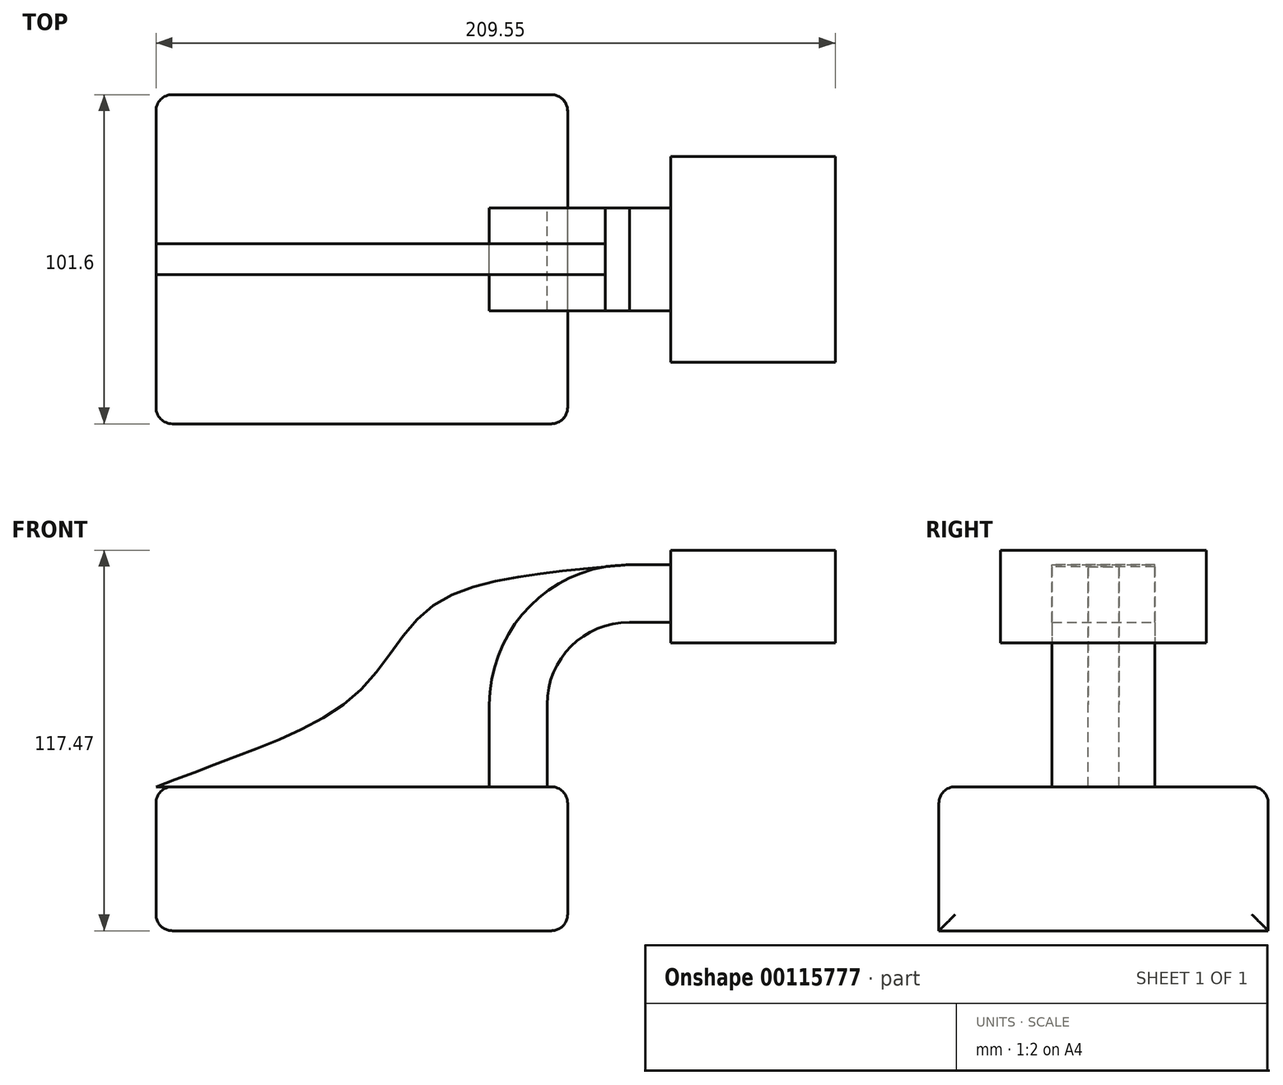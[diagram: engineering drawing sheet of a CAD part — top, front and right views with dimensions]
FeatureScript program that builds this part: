
annotation { "Feature Type Name" : "Feature", "Feature Type Description" : "" }
export const myFeature = defineFeature(function(context is Context, id is Id, definition is map)
    precondition{}
    {
        {
            var Q0;
            Q0=qCreatedBy(makeId("Front.planeOp"),FACE);
            var sketch = newSketch(context, id + "F0", { "sketchPlane" : qUnion([Q0])});
            skLineSegment(sketch, "E0.bottom", {"start": v(0, 0) * mm, "end": v(127, 0) * mm});
            skLineSegment(sketch, "E0.top", {"start": v(0, 44.45) * mm, "end": v(127, 44.45) * mm});
            skLineSegment(sketch, "E0.left", {"start": v(0, 0) * mm, "end": v(0, 44.45) * mm});
            skLineSegment(sketch, "E0.right", {"start": v(127, 0) * mm, "end": v(127, 44.45) * mm});
            skLineSegment(sketch, "E1.bottom", {"start": v(158.75, 88.9) * mm, "end": v(209.55, 88.9) * mm});
            skLineSegment(sketch, "E1.top", {"start": v(158.75, 117.48) * mm, "end": v(209.55, 117.48) * mm});
            skLineSegment(sketch, "E1.left", {"start": v(158.75, 88.9) * mm, "end": v(158.75, 117.48) * mm});
            skLineSegment(sketch, "E1.right", {"start": v(209.55, 88.9) * mm, "end": v(209.55, 117.48) * mm});
            skLineSegment(sketch, "E2", {"start": v(120.65, 44.45) * mm, "end": v(120.65, 69.85) * mm});
            skLineSegment(sketch, "E3", {"start": v(146.05, 95.25) * mm, "end": v(158.75, 95.25) * mm});
            skArc(sketch, "E4", {"start": v(120.65, 69.85) * mm, "mid": v(128.09, 87.81) * mm, "end": v(146.05, 95.25) * mm});
            skLineSegment(sketch, "E5.0", {"start": v(146.05, 113.03) * mm, "end": v(158.75, 113.03) * mm});
            skArc(sketch, "E5.1", {"start": v(102.87, 69.85) * mm, "mid": v(115.52, 100.38) * mm, "end": v(146.05, 113.03) * mm});
            skLineSegment(sketch, "E5.2", {"start": v(102.87, 44.45) * mm, "end": v(102.87, 69.85) * mm});
            skPoint(sketch, "E6", {"position": v(114.9, 109.67) * mm});
            skPoint(sketch, "E7", {"position": v(83.78, 99.03) * mm});
            skPoint(sketch, "E8", {"position": v(62.5, 73.65) * mm});
            skPoint(sketch, "E9", {"position": v(28.52, 55.23) * mm});
            skFitSpline(sketch, "E10", {"points": [v(0, 44.45) * mm, v(28.52, 55.23) * mm, v(62.5, 73.65) * mm, v(83.78, 99.03) * mm, v(114.9, 109.67) * mm, v(146.05, 113.03) * mm], "startDerivative": vector(142.18, 53.02) * mm, "endDerivative": vector(157.03, 13.52) * mm});
            skSolve(sketch);
        }
        {
            var Q0;
            Q0=makeQuery(id+"F0.imprint","IMPRINT",FACE,{"disambiguationData":[TD([[makeQuery(id+"F0.imprint","IMPRINT",EDGE,{"derivedFrom":sQuery(id+"F0.wireOp",EDGE,"E0.bottom")}),1.0]])]});
            extrude(context, id + "F1", {"entities" : qUnion([Q0]), "endBound" : BoundingType.SYMMETRIC, "depth" : 101.6 * mm});
        }
        {
            var Q0;
            {var subQ3=sQuery(id+"F0.wireOp",EDGE,"E1.bottom");Q0=makeQuery(id+"F0.imprint","IMPRINT",FACE,{"disambiguationData":[TD([[makeQuery(id+"F0.imprint","IMPRINT",EDGE,{"derivedFrom":subQ3}),1.0]])]});}
            extrude(context, id + "F2", {"entities" : qUnion([Q0]), "endBound" : BoundingType.SYMMETRIC, "depth" : 63.5 * mm});
        }
        {
            var Q0;
            {var subQ1=sQuery(id+"F0.wireOp",EDGE,"E2");Q0=makeQuery(id+"F0.imprint","IMPRINT",FACE,{"disambiguationData":[TD([[makeQuery(id+"F0.imprint","IMPRINT",EDGE,{"derivedFrom":subQ1}),1.0]])]});}
            extrude(context, id + "F3", {"entities" : qUnion([Q0]), "endBound" : BoundingType.SYMMETRIC, "depth" : 31.75 * mm});
        }
        {
            var Q0;
            {var subQ3=sQuery(id+"F0.wireOp",EDGE,"E5.2");Q0=makeQuery(id+"F0.imprint","IMPRINT",FACE,{"disambiguationData":[TD([[makeQuery(id+"F0.imprint","IMPRINT",EDGE,{"derivedFrom":subQ3}),1.0]])]});}
            extrude(context, id + "F4", {"entities" : qUnion([Q0]), "endBound" : BoundingType.SYMMETRIC, "depth" : 9.52 * mm});
        }
        {
            var Q0;
            Q0=makeQuery(id+"F1.opExtrude","SWEPT_FACE",FACE,{"disambiguationData":[OSD([sQuery(id+"F0.wireOp",EDGE,"E0.top")])]});
            fillet(context, id + "F5", {"entities" : qUnion([Q0]), "radius" : 5.08 * mm, "tangentPropagation" : true, "allowEdgeOverflow" : false});
        }
        {
            var Q0;
            Q0=makeQuery(id+"F1.opExtrude","SWEPT_FACE",FACE,{"disambiguationData":[OSD([sQuery(id+"F0.wireOp",EDGE,"E0.right")])]});
            fillet(context, id + "F6", {"entities" : qUnion([Q0]), "radius" : 5.08 * mm, "tangentPropagation" : true, "allowEdgeOverflow" : false});
        }
        {
            var Q0;
            Q0=makeQuery(id+"F1.opExtrude","SWEPT_FACE",FACE,{"disambiguationData":[OSD([sQuery(id+"F0.wireOp",EDGE,"E0.left")])]});
            fillet(context, id + "F7", {"entities" : qUnion([Q0]), "radius" : 5.08 * mm, "tangentPropagation" : true, "allowEdgeOverflow" : false});
        }
    });
